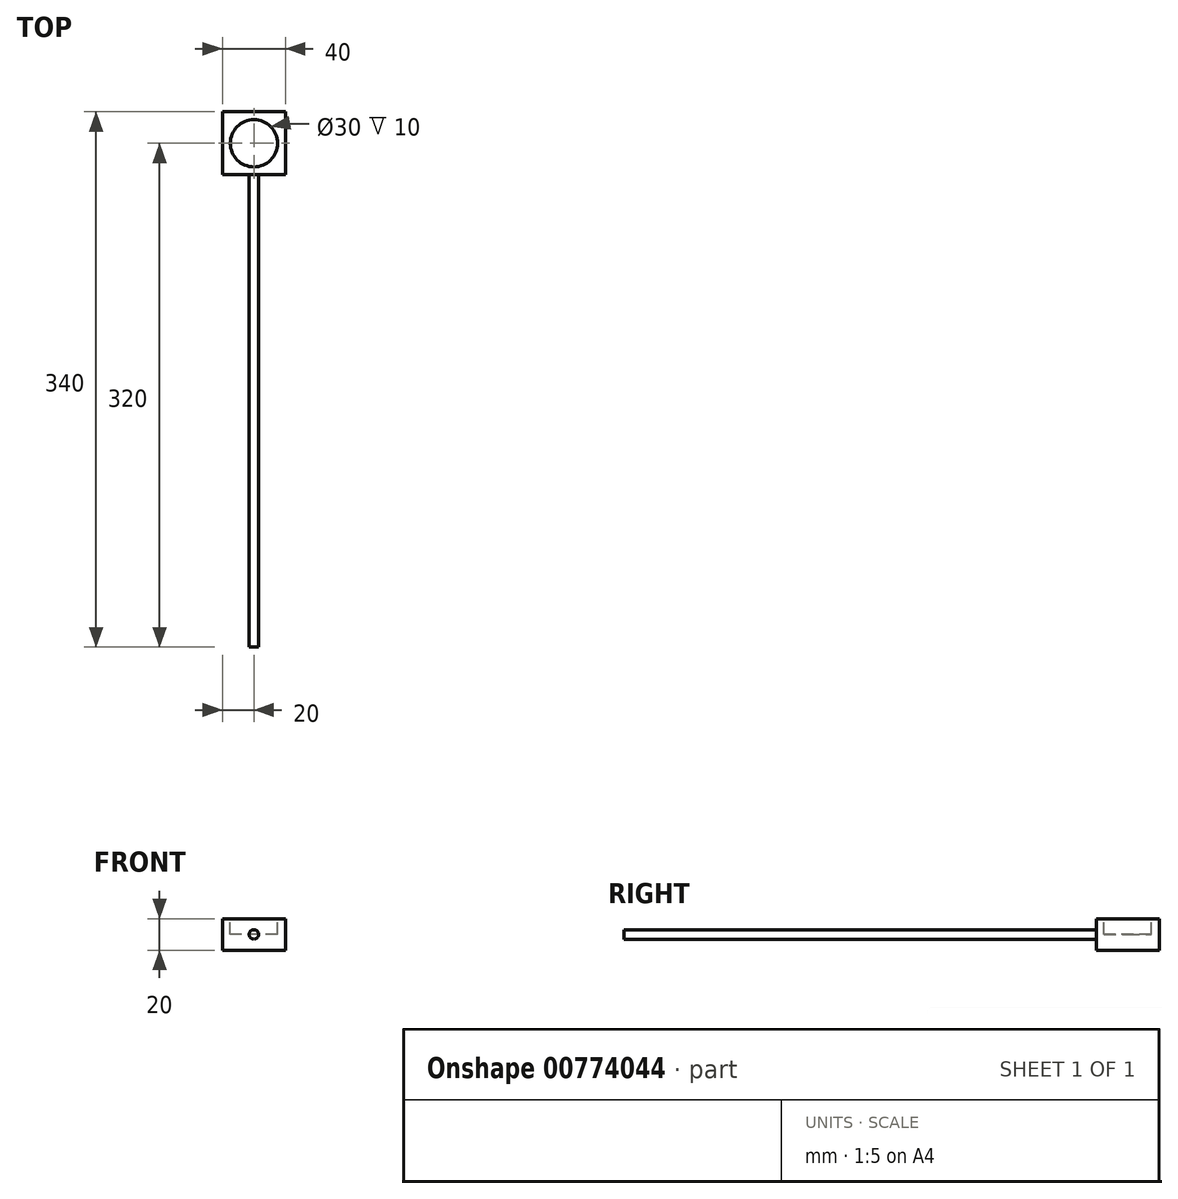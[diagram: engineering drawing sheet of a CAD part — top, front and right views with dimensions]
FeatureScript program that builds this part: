
annotation { "Feature Type Name" : "Feature", "Feature Type Description" : "" }
export const myFeature = defineFeature(function(context is Context, id is Id, definition is map)
    precondition{}
    {
        {
            var Q0;
            Q0=qCreatedBy(makeId("Front.planeOp"),FACE);
            var sketch = newSketch(context, id + "F0", { "sketchPlane" : qUnion([Q0])});
            skCircle(sketch, "E0", {"center": v(0, 0) * mm, "radius": 3 * mm});
            skSolve(sketch);
        }
        {
            var Q0;
            Q0 = qSketchRegion(id + "F0", true);
            extrude(context, id + "F1", {"entities" : qUnion([Q0]), "depth" : 340 * mm, "offsetDistance" : 25 * mm});
        }
        {
            var Q0;
            Q0=qCreatedBy(makeId("Front.planeOp"),FACE);
            var sketch = newSketch(context, id + "F2", { "sketchPlane" : qUnion([Q0])});
            skLineSegment(sketch, "E1.bottom", {"start": v(20, 10) * mm, "end": v(-20, 10) * mm});
            skLineSegment(sketch, "E1.top", {"start": v(20, -10) * mm, "end": v(-20, -10) * mm});
            skLineSegment(sketch, "E1.left", {"start": v(20, 10) * mm, "end": v(20, -10) * mm});
            skLineSegment(sketch, "E1.right", {"start": v(-20, 10) * mm, "end": v(-20, -10) * mm});
            skSolve(sketch);
        }
        {
            var Q0;
            Q0 = qSketchRegion(id + "F2", true);
            extrude(context, id + "F3", {"entities" : qUnion([Q0]), "operationType" : NewBodyOperationType.ADD, "depth" : 40 * mm, "offsetDistance" : 25 * mm});
        }
        {
            var Q0;
            Q0=makeQuery(id+"F3.opExtrude","SWEPT_FACE",FACE,{"disambiguationData":[OSD([sQuery(id+"F2.wireOp",EDGE,"E1.bottom")])]});
            var sketch = newSketch(context, id + "F4", { "sketchPlane" : qUnion([Q0])});
            skCircle(sketch, "E2", {"center": v(0, -20) * mm, "radius": 15 * mm});
            skPoint(sketch, "E2.centerSnap0", {"position": v(-20, -20) * mm});
            skSolve(sketch);
        }
        {
            var Q0;
            Q0 = qSketchRegion(id + "F4", true);
            extrude(context, id + "F5", {"entities" : qUnion([Q0]), "operationType" : NewBodyOperationType.REMOVE, "oppositeDirection" : true, "depth" : 10 * mm, "offsetDistance" : 25 * mm});
        }
    });
